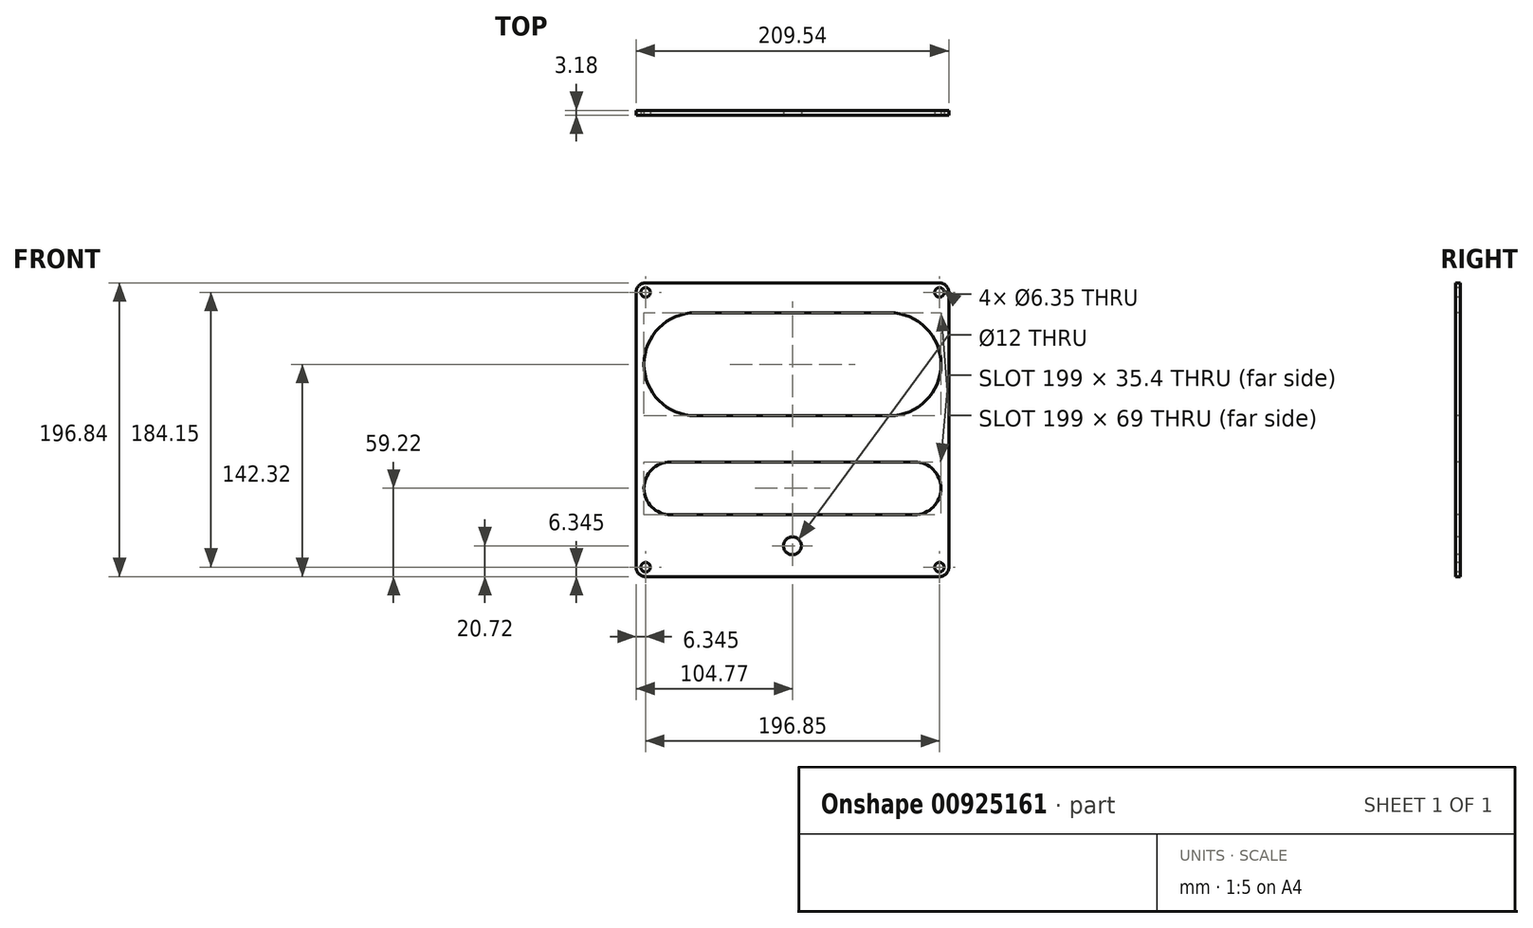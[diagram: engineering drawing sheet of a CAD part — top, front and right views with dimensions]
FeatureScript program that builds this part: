
annotation { "Feature Type Name" : "Feature", "Feature Type Description" : "" }
export const myFeature = defineFeature(function(context is Context, id is Id, definition is map)
    precondition{}
    {
        {
            var Q0;
            Q0=qCreatedBy(makeId("Front.planeOp"),FACE);
            var sketch = newSketch(context, id + "F0", { "sketchPlane" : qUnion([Q0])});
            skLineSegment(sketch, "E0.bottom", {"start": v(-98.43, 98.42) * mm, "end": v(98.43, 98.43) * mm});
            skLineSegment(sketch, "E0.top", {"start": v(-98.43, -98.43) * mm, "end": v(98.43, -98.43) * mm});
            skLineSegment(sketch, "E0.left", {"start": v(-104.78, 92.08) * mm, "end": v(-104.78, -92.08) * mm});
            skLineSegment(sketch, "E0.right", {"start": v(104.78, 92.08) * mm, "end": v(104.78, -92.08) * mm});
            skPoint(sketch, "E1.visualSharp", {"position": v(-104.78, 98.42) * mm});
            skArc(sketch, "E1.filletArc", {"start": v(-98.43, 98.42) * mm, "mid": v(-102.92, 96.57) * mm, "end": v(-104.77, 92.08) * mm});
            skPoint(sketch, "E2.visualSharp", {"position": v(104.78, 98.43) * mm});
            skArc(sketch, "E2.filletArc", {"start": v(104.77, 92.08) * mm, "mid": v(102.92, 96.57) * mm, "end": v(98.43, 98.42) * mm});
            skPoint(sketch, "E3.visualSharp", {"position": v(104.78, -98.43) * mm});
            skArc(sketch, "E3.filletArc", {"start": v(98.43, -98.43) * mm, "mid": v(102.92, -96.57) * mm, "end": v(104.78, -92.08) * mm});
            skPoint(sketch, "E4.visualSharp", {"position": v(-104.78, -98.43) * mm});
            skArc(sketch, "E4.filletArc", {"start": v(-104.78, -92.08) * mm, "mid": v(-102.92, -96.57) * mm, "end": v(-98.43, -98.43) * mm});
            skSolve(sketch);
        }
        {
            var Q0;
            Q0=qSketchRegion(id+"F0",true);
            extrude(context, id + "F1", {"entities" : qUnion([Q0]), "depth" : 3.17 * mm, "offsetDistance" : 25.4 * mm});
        }
        {
            var Q0;
            Q0=makeQuery(id+"F1.opExtrude","CAP_FACE",FACE,{"disambiguationData":[OSD([sQuery(id+"F0.wireOp",EDGE,"E0.bottom"),sQuery(id+"F0.wireOp",EDGE,"E0.top"),sQuery(id+"F0.wireOp",EDGE,"E0.left"),sQuery(id+"F0.wireOp",EDGE,"E0.right"),sQuery(id+"F0.wireOp",EDGE,"E1.filletArc"),sQuery(id+"F0.wireOp",EDGE,"E2.filletArc"),sQuery(id+"F0.wireOp",EDGE,"E3.filletArc"),sQuery(id+"F0.wireOp",EDGE,"E4.filletArc")])],"isStart":false});
            var sketch = newSketch(context, id + "F2", { "sketchPlane" : qUnion([Q0])});
            skCircle(sketch, "E5", {"center": v(-98.42, 92.08) * mm, "radius": 3.18 * mm});
            skCircle(sketch, "E6", {"center": v(98.42, 92.08) * mm, "radius": 3.18 * mm});
            skCircle(sketch, "E7", {"center": v(98.43, -92.08) * mm, "radius": 3.18 * mm});
            skCircle(sketch, "E8", {"center": v(-98.42, -92.08) * mm, "radius": 3.18 * mm});
            skSolve(sketch);
        }
        {
            var Q0;
            Q0=qSketchRegion(id+"F2",true);
            extrude(context, id + "F3", {"entities" : qUnion([Q0]), "operationType" : NewBodyOperationType.REMOVE, "oppositeDirection" : true, "depth" : 25.4 * mm, "offsetDistance" : 25.4 * mm});
        }
        {
            var Q0;
            Q0=makeQuery(id+"F1.opExtrude","CAP_FACE",FACE,{"disambiguationData":[OSD([sQuery(id+"F0.wireOp",EDGE,"E0.bottom"),sQuery(id+"F0.wireOp",EDGE,"E0.top"),sQuery(id+"F0.wireOp",EDGE,"E0.left"),sQuery(id+"F0.wireOp",EDGE,"E0.right"),sQuery(id+"F0.wireOp",EDGE,"E1.filletArc"),sQuery(id+"F0.wireOp",EDGE,"E2.filletArc"),sQuery(id+"F0.wireOp",EDGE,"E3.filletArc"),sQuery(id+"F0.wireOp",EDGE,"E4.filletArc")])],"isStart":false});
            var sketch = newSketch(context, id + "F4", { "sketchPlane" : qUnion([Q0])});
            skLineSegment(sketch, "E9", {"start": v(-104.78, 0) * mm, "end": v(-65, 0) * mm, "construction": true});
            skLineSegment(sketch, "E10", {"start": v(0, 98.43) * mm, "end": v(0, -98.43) * mm, "construction": true});
            skLineSegment(sketch, "E11.0", {"start": v(-119.48, 43.9) * mm, "end": v(90.07, 43.9) * mm, "construction": true});
            skLineSegment(sketch, "E12.0", {"start": v(-65, 9.4) * mm, "end": v(65, 9.4) * mm});
            skLineSegment(sketch, "E13.0", {"start": v(-65, 78.4) * mm, "end": v(65, 78.4) * mm});
            skLineSegment(sketch, "E14.0", {"start": v(-65, 101.21) * mm, "end": v(-65, 0) * mm, "construction": true});
            skArc(sketch, "E15", {"start": v(-65, 78.4) * mm, "mid": v(-99.5, 43.9) * mm, "end": v(-65, 9.4) * mm});
            skArc(sketch, "E16.MirrorCS", {"start": v(65, 78.4) * mm, "mid": v(99.5, 43.9) * mm, "end": v(65, 9.4) * mm});
            skLineSegment(sketch, "E17.MirrorCS", {"start": v(65, 101.21) * mm, "end": v(65, 0) * mm, "construction": true});
            skLineSegment(sketch, "E18.0", {"start": v(-104.78, -39.2) * mm, "end": v(104.78, -39.2) * mm, "construction": true});
            skLineSegment(sketch, "E19.0", {"start": v(-81.8, -56.9) * mm, "end": v(81.8, -56.9) * mm});
            skLineSegment(sketch, "E20.trimOffspring", {"start": v(0, 0) * mm, "end": v(104.78, 0) * mm, "construction": true});
            skPoint(sketch, "E21.trimOffspring.end.orphan", {"position": v(-65, -95.64) * mm});
            skPoint(sketch, "E22.trimOffspring.end.orphan", {"position": v(65, -95.64) * mm});
            skLineSegment(sketch, "E23.MirrorCS", {"start": v(-81.8, -21.5) * mm, "end": v(81.8, -21.5) * mm});
            skLineSegment(sketch, "E24.0", {"start": v(-81.8, 98.43) * mm, "end": v(-81.8, -98.43) * mm, "construction": true});
            skArc(sketch, "E25", {"start": v(-81.8, -21.5) * mm, "mid": v(-99.5, -39.2) * mm, "end": v(-81.8, -56.9) * mm});
            skPoint(sketch, "E25.startSnap0", {"position": v(-81.8, 0) * mm});
            skPoint(sketch, "E26.orphan", {"position": v(-104.78, -56.9) * mm});
            skPoint(sketch, "E27.orphan", {"position": v(-104.78, -21.5) * mm});
            skArc(sketch, "E28.MirrorCS", {"start": v(81.8, -21.5) * mm, "mid": v(99.5, -39.2) * mm, "end": v(81.8, -56.9) * mm});
            skPoint(sketch, "E29.orphan", {"position": v(104.78, -56.9) * mm});
            skPoint(sketch, "E30.orphan", {"position": v(104.78, -21.5) * mm});
            skLineSegment(sketch, "E31.0", {"start": v(61.6, 98.43) * mm, "end": v(61.6, -98.43) * mm, "construction": true});
            skPoint(sketch, "E32.orphan", {"position": v(104.78, -52.3) * mm});
            skPoint(sketch, "E33.orphan", {"position": v(104.78, -74.3) * mm});
            skPoint(sketch, "E34.MirrorCS.end.orphan", {"position": v(61.6, -74.3) * mm});
            skPoint(sketch, "E34.MirrorCS.start.orphan", {"position": v(0, -74.3) * mm});
            skPoint(sketch, "E35.0.start.orphan", {"position": v(0, -52.3) * mm});
            skPoint(sketch, "E36.start.orphan", {"position": v(61.6, -52.3) * mm});
            skPoint(sketch, "E37.orphan", {"position": v(-61.6, -74.3) * mm});
            skPoint(sketch, "E38.MirrorCS.end.orphan", {"position": v(-61.6, -52.3) * mm});
            skSolve(sketch);
        }
        {
            var Q0;
            Q0 = qSketchRegion(id + "F4", true);
            extrude(context, id + "F5", {"entities" : qUnion([Q0]), "operationType" : NewBodyOperationType.REMOVE, "oppositeDirection" : true, "depth" : 25 * mm, "offsetDistance" : 25 * mm});
        }
        {
            var Q0;
            Q0 = qSketchRegion(id + "F4", true);
            extrude(context, id + "F6", {"entities" : qUnion([Q0]), "operationType" : NewBodyOperationType.REMOVE, "oppositeDirection" : true, "depth" : 25 * mm, "offsetDistance" : 25 * mm});
        }
        {
            var Q0;
            Q0 = qSketchRegion(id + "F4", true);
            extrude(context, id + "F7", {"entities" : qUnion([Q0]), "operationType" : NewBodyOperationType.REMOVE, "oppositeDirection" : true, "depth" : 25 * mm, "offsetDistance" : 25 * mm});
        }
        {
            var Q0;
            Q0=makeQuery(id+"F1.opExtrude","CAP_FACE",FACE,{"disambiguationData":[OSD([sQuery(id+"F0.wireOp",EDGE,"E0.bottom"),sQuery(id+"F0.wireOp",EDGE,"E0.top"),sQuery(id+"F0.wireOp",EDGE,"E0.left"),sQuery(id+"F0.wireOp",EDGE,"E0.right"),sQuery(id+"F0.wireOp",EDGE,"E1.filletArc"),sQuery(id+"F0.wireOp",EDGE,"E2.filletArc"),sQuery(id+"F0.wireOp",EDGE,"E3.filletArc"),sQuery(id+"F0.wireOp",EDGE,"E4.filletArc")])],"isStart":false});
            var sketch = newSketch(context, id + "F8", { "sketchPlane" : qUnion([Q0])});
            skCircle(sketch, "E39", {"center": v(0, -77.7) * mm, "radius": 6 * mm});
            skSolve(sketch);
        }
        {
            var Q0;
            Q0 = qSketchRegion(id + "F8", true);
            extrude(context, id + "F9", {"entities" : qUnion([Q0]), "operationType" : NewBodyOperationType.REMOVE, "oppositeDirection" : true, "depth" : 25 * mm, "offsetDistance" : 25 * mm});
        }
    });
